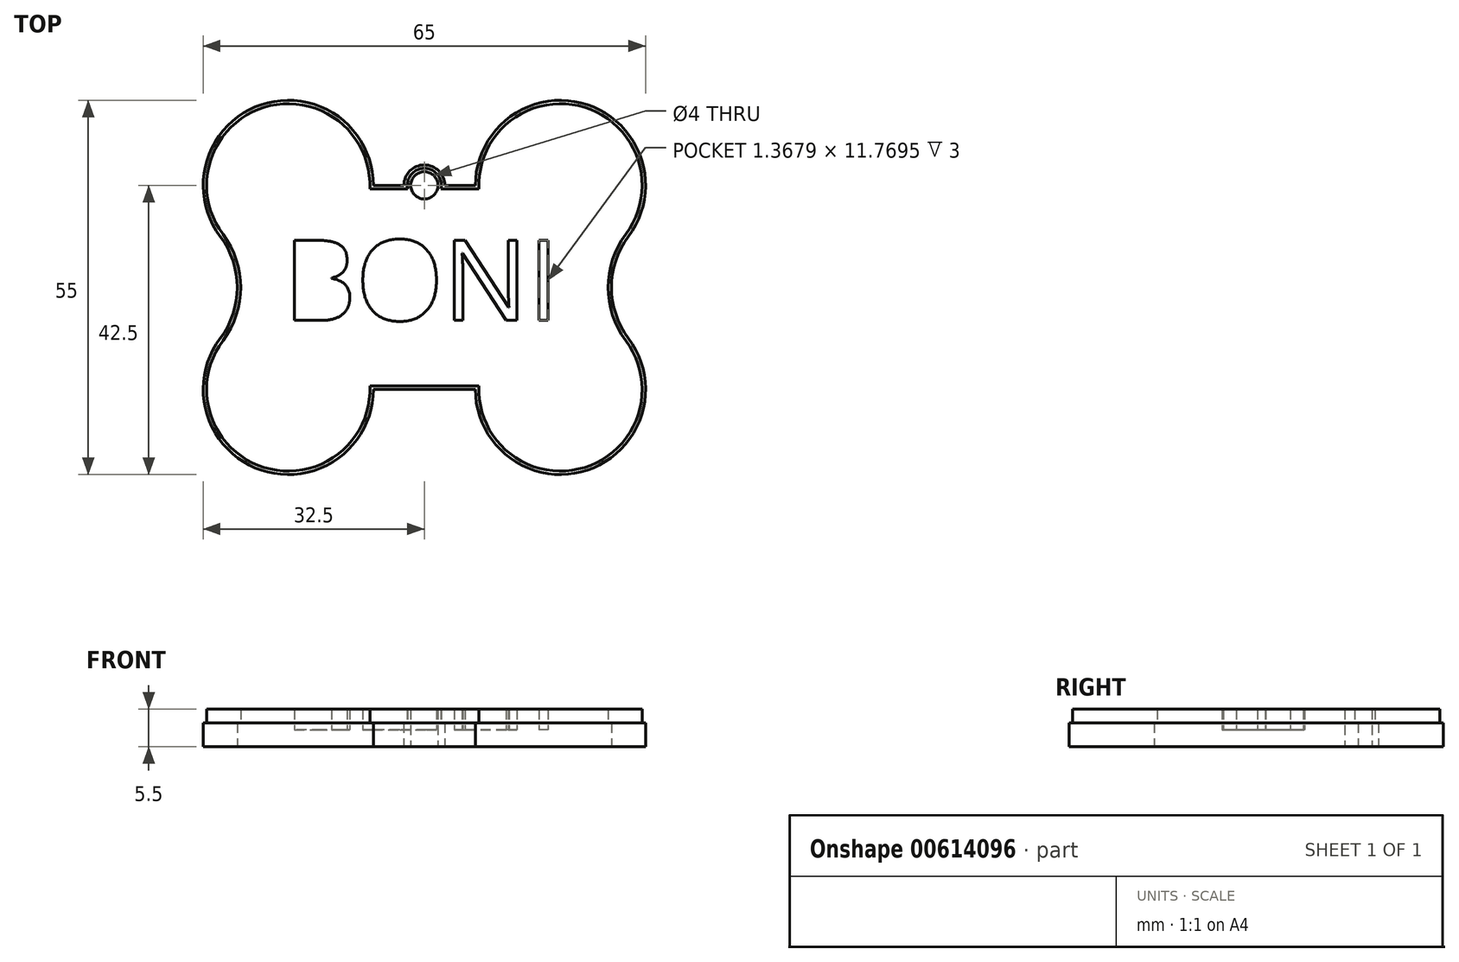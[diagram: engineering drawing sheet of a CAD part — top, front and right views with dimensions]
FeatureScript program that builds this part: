
annotation { "Feature Type Name" : "Feature", "Feature Type Description" : "" }
export const myFeature = defineFeature(function(context is Context, id is Id, definition is map)
    precondition{}
    {
        {
            var Q0;
            Q0=qCreatedBy(makeId("Top.planeOp"),FACE);
            var sketch = newSketch(context, id + "F0", { "sketchPlane" : qUnion([Q0])});
            skPoint(sketch, "E0.end.orphan", {"position": v(0, 30) * mm});
            skArc(sketch, "E1", {"start": v(22.5, 30) * mm, "mid": v(6.05, 41.86) * mm, "end": v(0, 22.5) * mm});
            skArc(sketch, "E2", {"start": v(60, 22.5) * mm, "mid": v(53.95, 41.86) * mm, "end": v(37.5, 30) * mm});
            skArc(sketch, "E3", {"start": v(37.5, 0) * mm, "mid": v(53.95, -11.86) * mm, "end": v(60, 7.5) * mm});
            skArc(sketch, "E4", {"start": v(0, 7.5) * mm, "mid": v(6.05, -11.86) * mm, "end": v(22.5, 0) * mm});
            skPoint(sketch, "E5.first.point", {"position": v(0, 22.5) * mm});
            skPoint(sketch, "E5.second.point", {"position": v(0, 7.5) * mm});
            skArc(sketch, "E6", {"start": v(0, 7.5) * mm, "mid": v(2.5, 15) * mm, "end": v(0, 22.5) * mm});
            skArc(sketch, "E7", {"start": v(60, 22.5) * mm, "mid": v(57.5, 15) * mm, "end": v(60, 7.5) * mm});
            skPoint(sketch, "E7.first.point", {"position": v(60, 22.5) * mm});
            skPoint(sketch, "E7.second.point", {"position": v(60, 7.5) * mm});
            skPoint(sketch, "E8.start.orphan", {"position": v(60, 0) * mm});
            skPoint(sketch, "E9.trimOffspring.end.orphan", {"position": v(0, 0) * mm});
            skLineSegment(sketch, "E10", {"start": v(22.5, 0) * mm, "end": v(37.5, 0) * mm});
            skArc(sketch, "E11", {"start": v(32, 30) * mm, "mid": v(30, 32) * mm, "end": v(28, 30) * mm, "construction": true});
            skCircle(sketch, "E12", {"center": v(30, 30) * mm, "radius": 2 * mm});
            skArc(sketch, "E13", {"start": v(33, 30) * mm, "mid": v(30, 33) * mm, "end": v(27, 30) * mm});
            skLineSegment(sketch, "E14.trimOffspring", {"start": v(33, 30) * mm, "end": v(37.5, 30) * mm});
            skLineSegment(sketch, "E15", {"start": v(22.5, 30) * mm, "end": v(27, 30) * mm});
            skSolve(sketch);
        }
        {
            var Q0;
            Q0 = qSketchRegion(id + "F0", true);
            extrude(context, id + "F1", {"entities" : qUnion([Q0]), "depth" : 3.5 * mm, "offsetDistance" : 25 * mm});
        }
        {
            var Q0;
            Q0=makeQuery(id+"F1.opExtrude","CAP_FACE",FACE,{"disambiguationData":[OSD([sQuery(id+"F0.wireOp",EDGE,"E1"),sQuery(id+"F0.wireOp",EDGE,"E2"),sQuery(id+"F0.wireOp",EDGE,"E3"),sQuery(id+"F0.wireOp",EDGE,"E4"),sQuery(id+"F0.wireOp",EDGE,"E6"),sQuery(id+"F0.wireOp",EDGE,"E7"),sQuery(id+"F0.wireOp",EDGE,"E10"),sQuery(id+"F0.wireOp",EDGE,"52539e43-6132-47ac-8ffe-d8ec62cebe2f.sketch_text.stroke-0"),sQuery(id+"F0.wireOp",EDGE,"52539e43-6132-47ac-8ffe-d8ec62cebe2f.sketch_text.stroke-1"),sQuery(id+"F0.wireOp",EDGE,"52539e43-6132-47ac-8ffe-d8ec62cebe2f.sketch_text.stroke-2"),sQuery(id+"F0.wireOp",EDGE,"52539e43-6132-47ac-8ffe-d8ec62cebe2f.sketch_text.stroke-3"),sQuery(id+"F0.wireOp",EDGE,"52539e43-6132-47ac-8ffe-d8ec62cebe2f.sketch_text.stroke-4"),sQuery(id+"F0.wireOp",EDGE,"52539e43-6132-47ac-8ffe-d8ec62cebe2f.sketch_text.stroke-5"),sQuery(id+"F0.wireOp",EDGE,"52539e43-6132-47ac-8ffe-d8ec62cebe2f.sketch_text.stroke-6"),sQuery(id+"F0.wireOp",EDGE,"52539e43-6132-47ac-8ffe-d8ec62cebe2f.sketch_text.stroke-7"),sQuery(id+"F0.wireOp",EDGE,"52539e43-6132-47ac-8ffe-d8ec62cebe2f.sketch_text.stroke-8"),sQuery(id+"F0.wireOp",EDGE,"52539e43-6132-47ac-8ffe-d8ec62cebe2f.sketch_text.stroke-9"),sQuery(id+"F0.wireOp",EDGE,"52539e43-6132-47ac-8ffe-d8ec62cebe2f.sketch_text.stroke-10"),sQuery(id+"F0.wireOp",EDGE,"52539e43-6132-47ac-8ffe-d8ec62cebe2f.sketch_text.stroke-25"),sQuery(id+"F0.wireOp",EDGE,"52539e43-6132-47ac-8ffe-d8ec62cebe2f.sketch_text.stroke-26"),sQuery(id+"F0.wireOp",EDGE,"52539e43-6132-47ac-8ffe-d8ec62cebe2f.sketch_text.stroke-27"),sQuery(id+"F0.wireOp",EDGE,"52539e43-6132-47ac-8ffe-d8ec62cebe2f.sketch_text.stroke-28"),sQuery(id+"F0.wireOp",EDGE,"52539e43-6132-47ac-8ffe-d8ec62cebe2f.sketch_text.stroke-29"),sQuery(id+"F0.wireOp",EDGE,"52539e43-6132-47ac-8ffe-d8ec62cebe2f.sketch_text.stroke-30"),sQuery(id+"F0.wireOp",EDGE,"52539e43-6132-47ac-8ffe-d8ec62cebe2f.sketch_text.stroke-31"),sQuery(id+"F0.wireOp",EDGE,"52539e43-6132-47ac-8ffe-d8ec62cebe2f.sketch_text.stroke-32"),sQuery(id+"F0.wireOp",EDGE,"52539e43-6132-47ac-8ffe-d8ec62cebe2f.sketch_text.stroke-41"),sQuery(id+"F0.wireOp",EDGE,"52539e43-6132-47ac-8ffe-d8ec62cebe2f.sketch_text.stroke-42"),sQuery(id+"F0.wireOp",EDGE,"52539e43-6132-47ac-8ffe-d8ec62cebe2f.sketch_text.stroke-43"),sQuery(id+"F0.wireOp",EDGE,"52539e43-6132-47ac-8ffe-d8ec62cebe2f.sketch_text.stroke-44"),sQuery(id+"F0.wireOp",EDGE,"52539e43-6132-47ac-8ffe-d8ec62cebe2f.sketch_text.stroke-45"),sQuery(id+"F0.wireOp",EDGE,"52539e43-6132-47ac-8ffe-d8ec62cebe2f.sketch_text.stroke-46"),sQuery(id+"F0.wireOp",EDGE,"52539e43-6132-47ac-8ffe-d8ec62cebe2f.sketch_text.stroke-47"),sQuery(id+"F0.wireOp",EDGE,"52539e43-6132-47ac-8ffe-d8ec62cebe2f.sketch_text.stroke-48"),sQuery(id+"F0.wireOp",EDGE,"52539e43-6132-47ac-8ffe-d8ec62cebe2f.sketch_text.stroke-49"),sQuery(id+"F0.wireOp",EDGE,"52539e43-6132-47ac-8ffe-d8ec62cebe2f.sketch_text.stroke-50"),sQuery(id+"F0.wireOp",EDGE,"52539e43-6132-47ac-8ffe-d8ec62cebe2f.sketch_text.stroke-51"),sQuery(id+"F0.wireOp",EDGE,"52539e43-6132-47ac-8ffe-d8ec62cebe2f.sketch_text.stroke-52"),sQuery(id+"F0.wireOp",EDGE,"52539e43-6132-47ac-8ffe-d8ec62cebe2f.sketch_text.stroke-53"),sQuery(id+"F0.wireOp",EDGE,"52539e43-6132-47ac-8ffe-d8ec62cebe2f.sketch_text.stroke-54"),sQuery(id+"F0.wireOp",EDGE,"52539e43-6132-47ac-8ffe-d8ec62cebe2f.sketch_text.stroke-55"),sQuery(id+"F0.wireOp",EDGE,"52539e43-6132-47ac-8ffe-d8ec62cebe2f.sketch_text.stroke-56"),sQuery(id+"F0.wireOp",EDGE,"52539e43-6132-47ac-8ffe-d8ec62cebe2f.sketch_text.stroke-57"),sQuery(id+"F0.wireOp",EDGE,"52539e43-6132-47ac-8ffe-d8ec62cebe2f.sketch_text.stroke-58"),sQuery(id+"F0.wireOp",EDGE,"52539e43-6132-47ac-8ffe-d8ec62cebe2f.sketch_text.stroke-59"),sQuery(id+"F0.wireOp",EDGE,"E12"),sQuery(id+"F0.wireOp",EDGE,"E13"),sQuery(id+"F0.wireOp",EDGE,"E14.trimOffspring"),sQuery(id+"F0.wireOp",EDGE,"E15")])],"isStart":false});
            var sketch = newSketch(context, id + "F2", { "sketchPlane" : qUnion([Q0])});
            skArc(sketch, "E16.0", {"start": v(38.01, 0.5) * mm, "mid": v(53.56, -11.46) * mm, "end": v(59.6, 7.2) * mm});
            skLineSegment(sketch, "E16.1", {"start": v(21.99, 0.5) * mm, "end": v(38.01, 0.5) * mm});
            skArc(sketch, "E16.2", {"start": v(59.6, 7.2) * mm, "mid": v(57, 15) * mm, "end": v(59.6, 22.8) * mm});
            skArc(sketch, "E16.3", {"start": v(0.4, 7.2) * mm, "mid": v(6.44, -11.46) * mm, "end": v(21.99, 0.5) * mm});
            skArc(sketch, "E16.4", {"start": v(0.4, 22.8) * mm, "mid": v(3, 15) * mm, "end": v(0.4, 7.2) * mm});
            skArc(sketch, "E16.5", {"start": v(21.99, 29.5) * mm, "mid": v(6.44, 41.46) * mm, "end": v(0.4, 22.8) * mm});
            skArc(sketch, "E16.6", {"start": v(59.6, 22.8) * mm, "mid": v(53.56, 41.46) * mm, "end": v(38.01, 29.5) * mm});
            skLineSegment(sketch, "E16.7", {"start": v(38.01, 29.5) * mm, "end": v(32.45, 29.5) * mm});
            skArc(sketch, "E16.8", {"start": v(32.45, 29.5) * mm, "mid": v(30, 32.5) * mm, "end": v(27.55, 29.5) * mm});
            skLineSegment(sketch, "E16.9", {"start": v(27.55, 29.5) * mm, "end": v(21.99, 29.5) * mm});
            skSolve(sketch);
        }
        {
            var Q0;
            Q0=makeQuery(id+"F2.imprint","IMPRINT",FACE,{"disambiguationData":[TD([[makeQuery(id+"F2.imprint","IMPRINT",EDGE,{"derivedFrom":sQuery(id+"F2.wireOp",EDGE,"E16.0")}),1.0]])]});
            extrude(context, id + "F3", {"entities" : qUnion([Q0]), "operationType" : NewBodyOperationType.REMOVE, "oppositeDirection" : true, "depth" : 1 * mm, "offsetDistance" : 25 * mm});
        }
        {
            var Q0;
            Q0=makeQuery(id+"F3.boolean.opBoolean","COPY",FACE,{"derivedFrom":makeQuery(id+"F3.opExtrude","CAP_FACE",FACE,{"disambiguationData":[OSD([sQuery(id+"F2.wireOp",EDGE,"E16.0"),sQuery(id+"F2.wireOp",EDGE,"E16.1"),sQuery(id+"F2.wireOp",EDGE,"E16.2"),sQuery(id+"F2.wireOp",EDGE,"E16.3"),sQuery(id+"F2.wireOp",EDGE,"E16.4"),sQuery(id+"F2.wireOp",EDGE,"E16.5"),sQuery(id+"F2.wireOp",EDGE,"E16.6"),sQuery(id+"F2.wireOp",EDGE,"E16.7"),sQuery(id+"F2.wireOp",EDGE,"E16.8"),sQuery(id+"F2.wireOp",EDGE,"E16.9")])],"isStart":false})});
            var sketch = newSketch(context, id + "F4", { "sketchPlane" : qUnion([Q0])});
            skText(sketch, "E17", { "text": "BONI\n", "fontName": "OpenSans-Regular.ttf"});
            const initialGuessF4  = {"E17": [0.00927, 0.01016, 1, 0, 0.01187]};
            skSetInitialGuess(sketch, initialGuessF4);
            skSolve(sketch);
        }
        {
            var Q0;
            Q0=makeQuery(id+"F4.imprint","IMPRINT",FACE,{"disambiguationData":[TD([[makeQuery(id+"F4.imprint","IMPRINT",EDGE,{"derivedFrom":sQuery(id+"F4.wireOp",EDGE,"E17.sketch_text.stroke-0")}),1.0]])]});
            extrude(context, id + "F5", {"entities" : qUnion([Q0]), "operationType" : NewBodyOperationType.ADD, "depth" : 3 * mm, "offsetDistance" : 25 * mm});
        }
    });
